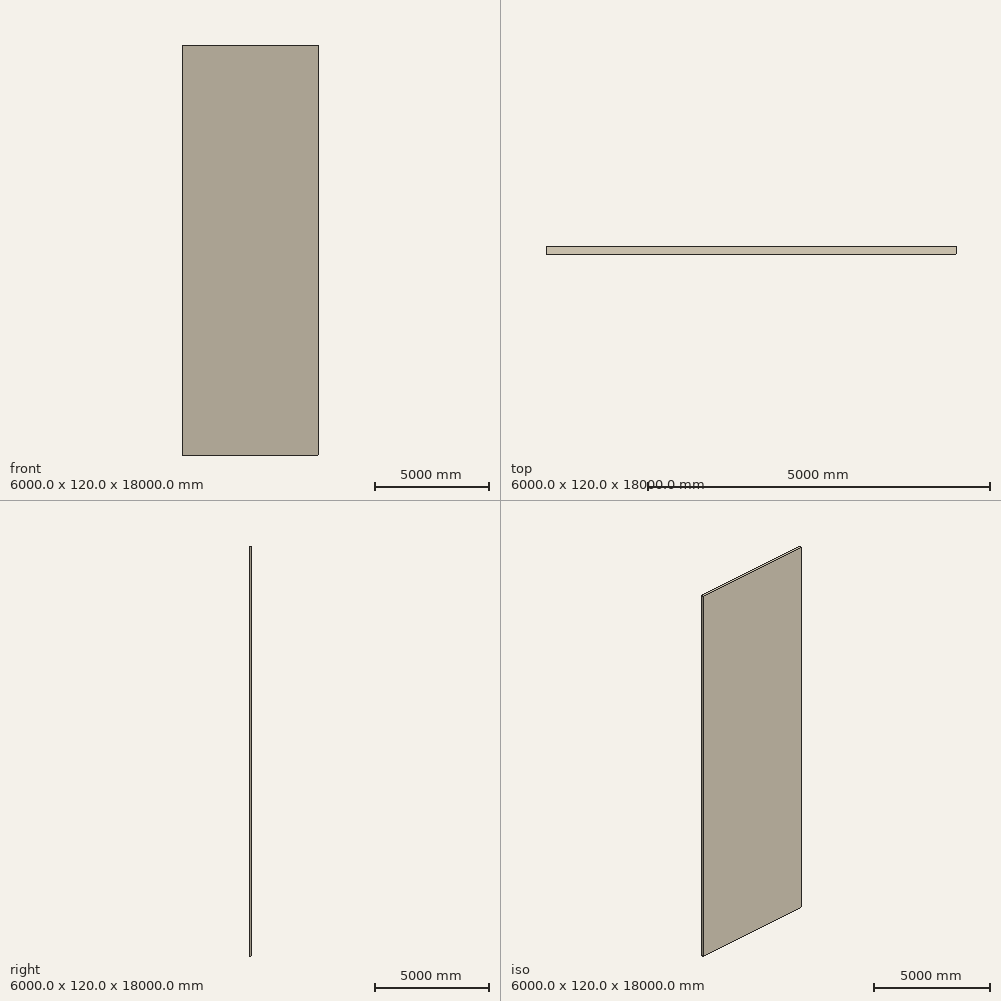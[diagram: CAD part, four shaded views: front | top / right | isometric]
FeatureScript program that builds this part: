
annotation { "Feature Type Name" : "Feature", "Feature Type Description" : "" }
export const myFeature = defineFeature(function(context is Context, id is Id, definition is map)
    precondition{}
    {
        {
            var Q0;
            Q0=qCreatedBy(makeId("Front.planeOp"),FACE);
            var sketch = newSketch(context, id + "F0", { "sketchPlane" : qUnion([Q0])});
            skLineSegment(sketch, "E0.bottom", {"start": v(-2998.87, 13671.7) * mm, "end": v(3001.13, 13671.7) * mm});
            skLineSegment(sketch, "E0.top", {"start": v(-2998.87, -4328.3) * mm, "end": v(3001.13, -4328.3) * mm});
            skLineSegment(sketch, "E0.left", {"start": v(-2998.87, 13671.7) * mm, "end": v(-2998.87, -4328.3) * mm});
            skLineSegment(sketch, "E0.right", {"start": v(3001.13, 13671.7) * mm, "end": v(3001.13, -4328.3) * mm});
            skSolve(sketch);
        }
        {
            var Q0;
            Q0=makeQuery(id+"F0.imprint","IMPRINT",FACE,{"disambiguationData":[TD([[makeQuery(id+"F0.imprint","IMPRINT",EDGE,{"derivedFrom":sQuery(id+"F0.wireOp",EDGE,"E0.bottom")}),-1.0]])]});
            extrude(context, id + "F1", {"entities" : qUnion([Q0]), "endBound" : BoundingType.SYMMETRIC, "depth" : 120 * mm, "offsetDistance" : 25 * mm});
        }
    });
